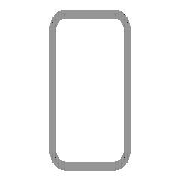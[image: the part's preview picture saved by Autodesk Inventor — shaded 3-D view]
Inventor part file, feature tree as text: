
AUTODESK INVENTOR PART (.ipt)
format: ipt  version: 2025.3 (Build 293356000, 356)  size: 133,120 bytes
history: native  units: mm (DEFAULTED — no unit token found)
features: other x4, sketch x1, plane x1
ambient origin geometry x8: Origin, YZ Plane, XZ Plane, XY Plane, X Axis, Y Axis, Z Axis, Center Point
bodies: Solid1 (feature_tree), Body (feature_tree)
feature tree (6):
  parser-record x1  (decoder bookkeeping rows leaked as tree rows — omitted from the tree; the rows remain in map.json)
  other  "Driven Length"
  other  "Start Plane"
  other  "End Plane"
  sketch  "Sketch3"  dims[d3=2040.0mm d4=0.0mm d7=6.0mm d9=40.0mm d11=80.0mm d12=3.0mm d13=80.0mm d14=2120.0mm d15=20.0mm d16=40.0mm d17=90.0deg d18=2040.0mm]
  plane  "Work Plane3"
